# Revit family: PRD_AR_ClthsHks_CoatHook_HDTX692,HDTX693
name_source: partatom
category: Plumbing Fixtures
revit_build: Autodesk Revit 2018 (Build: 20190510_1515(x64)
units: mm (PartAtom-declared; Revit-internal decimal feet)

## family parameters
Cut with Voids When Loaded = No
Host = Face
OmniClass Number = 23.40.00.00
OmniClass Title = Equipment and Furnishings
Part Type = Normal
Room Calculation Point = No
Round Connector Dimension = Use Diameter
Shared = No

## types (2) — shared parameters
AssetType = Fixed
Category = Pr_40_30_78_15, Clothes hooks
Color = Stainless steel
Default Elevation = 1050 mm
DurationUnit = year
Features = stainless steel, satin finished
Finish = Satin finished
HookMaterial = PRD_AR_StainlessSteel_Polished
IfcExportAs = IfcFurnitureType
IfcExportType = NOTDEFINED
MainColor = Stainless steel
Manufacturer = KWC Group AG
ManufacturerName = KWC Group AG
ManufacturerURL = www.kwc.com
Material = STAINLESS-STEEL
MaterialCode = 1.4301
MaterialThickness = 2.00 mm
NBSDescription = Clothes hooks
NBSReference = 45-35-72/322
NominalDepth = 22 mm  [stored 0.0721785 ft]
NominalHeight = 108 mm  [stored 0.354331 ft]
NominalWidth = 108 mm  [stored 0.354331 ft]
NumberOfHooks = 1
ProductInformation = https://pim.kwc.com
Size = 108x108x22 mm
SpecialFuncionality = ANTI-LIGATURE
SurfaceFinish = SATIN-FINISHED
SurfaceMaterial = PRD_AR_StainlessSteel_SatinFinished
TypeOfFixing = SCREW
URL = www.kwc.com
Uniclass2015Code = Pr_40_30_78_15
Uniclass2015Title = Clothes hooks
Uniclass2015Version = Products v1.10
Version = 1
WarrantyDurationUnit = year

## per-type parameters (varying)
| type | BIMObjectName | Bolts | Description | GrossWeight | ModelNumber | Name | NetWeight | TypeOfMounting |
| HDTX692 | PRD_AR_ClthsHks_CoatHook_HDTX692 | No | Coat hook, stainless steel, material thickness 2 mm, visible surface satin finished. Safety hook tilts downwards when overloaded,
projection 30 mm from wall plate. Dimensions 108 x 108 x 52 mm (W x H x D). | 0.50 kg | 2000090046 | Coat Hook HDTX692 | 0.48 kg | WALL-MOUNTING |
| HDTX693 | PRD_AR_ClthsHks_CoatHook_HDTX693 | Yes | Coat hook, stainless steel, material thickness 2 mm, visible surface satin finished. Safety hook tilts downwards when overloaded,
projection 30 mm from wall plate. Dimensions 108 x 108 x 52 mm (W x H x D). Model for mounting from behind with threaded bolts for vandalism-resistant mounting from a service room. | 1.32 kg | 2000090047 | Coat Hook HDTX693 | 1.25 kg | BOLT-MOUNTING |

note: column(s) folded — value = type name in every type: Model, ModelReference

note: [stored X ft] marks values corroborated as IEEE doubles in the binary element streams (Revit-internal decimal feet)
